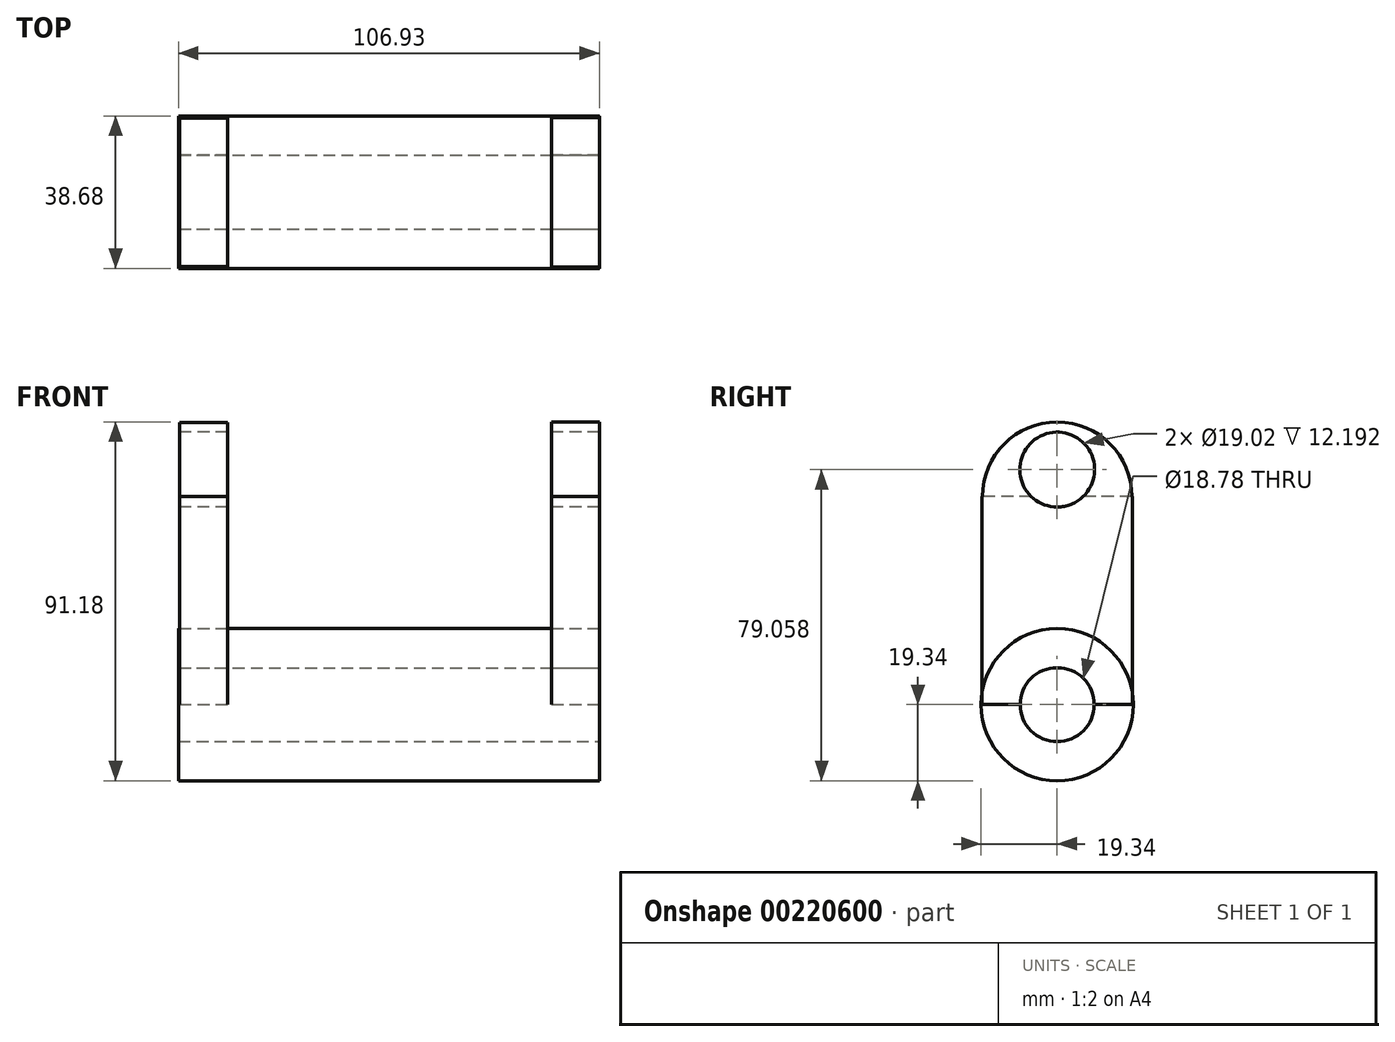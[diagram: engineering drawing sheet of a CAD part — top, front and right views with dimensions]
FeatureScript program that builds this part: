
annotation { "Feature Type Name" : "Feature", "Feature Type Description" : "" }
export const myFeature = defineFeature(function(context is Context, id is Id, definition is map)
    precondition{}
    {
        {
            var Q0;
            Q0=qCreatedBy(makeId("Top.planeOp"),FACE);
            var sketch = newSketch(context, id + "F0", { "sketchPlane" : qUnion([Q0])});
            skLineSegment(sketch, "E0.bottom", {"start": v(41.16, 19.13) * mm, "end": v(53.34, 19.13) * mm});
            skLineSegment(sketch, "E0.top", {"start": v(41.16, -19.13) * mm, "end": v(53.34, -19.13) * mm});
            skLineSegment(sketch, "E0.left", {"start": v(41.16, 19.13) * mm, "end": v(41.16, -19.13) * mm});
            skLineSegment(sketch, "E0.right", {"start": v(53.34, 19.13) * mm, "end": v(53.34, -19.13) * mm});
            skPoint(sketch, "E0.middle", {"position": v(47.25, 0) * mm});
            skLineSegment(sketch, "E1.MirrorCS", {"start": v(-41.16, 19.13) * mm, "end": v(-41.16, -19.13) * mm});
            skLineSegment(sketch, "E2.MirrorCS", {"start": v(-53.34, 19.13) * mm, "end": v(-53.34, -19.13) * mm});
            skLineSegment(sketch, "E3.MirrorCS", {"start": v(-41.16, 19.13) * mm, "end": v(-53.34, 19.13) * mm});
            skLineSegment(sketch, "E4.MirrorCS", {"start": v(-41.16, -19.13) * mm, "end": v(-53.34, -19.13) * mm});
            skSolve(sketch);
        }
        {
            var Q0;
            Q0=makeQuery(id+"F0.imprint","IMPRINT",FACE,{"disambiguationData":[TD([[makeQuery(id+"F0.imprint","IMPRINT",EDGE,{"derivedFrom":sQuery(id+"F0.wireOp",EDGE,"E0.bottom")}),-1.0]])]});
            var Q1;
            Q1=makeQuery(id+"F0.imprint","IMPRINT",FACE,{"disambiguationData":[TD([[makeQuery(id+"F0.imprint","IMPRINT",EDGE,{"derivedFrom":sQuery(id+"F0.wireOp",EDGE,"E1.MirrorCS")}),-1.0]])]});
            extrude(context, id + "F1", {"entities" : qUnion([Q0, Q1]), "depth" : 52.83 * mm});
        }
        {
            var Q0;
            Q0=makeQuery(id+"F1.opExtrude","SWEPT_FACE",FACE,{"disambiguationData":[OSD([sQuery(id+"F0.wireOp",EDGE,"E0.right")])]});
            var sketch = newSketch(context, id + "F2", { "sketchPlane" : qUnion([Q0])});
            skCircle(sketch, "E5", {"center": v(0, 0) * mm, "radius": 19.34 * mm});
            skSolve(sketch);
        }
        {
            var Q0;
            {var subQ1=sQuery(id+"F0.wireOp",EDGE,"E0.right");var subQ6=makeQuery(id+"F1.opExtrude","CAP_EDGE",EDGE,{"disambiguationData":[OSD([subQ1])],"isStart":true});Q0=makeQuery(id+"F2.imprint","IMPRINT",FACE,{"disambiguationData":[TD([[makeQuery(id+"F2.imprint","IMPRINT",EDGE,{"derivedFrom":subQ6}),-1.0]])]});}
            var Q1;
            {var subQ1=sQuery(id+"F0.wireOp",EDGE,"E0.right");var subQ6=makeQuery(id+"F1.opExtrude","CAP_EDGE",EDGE,{"disambiguationData":[OSD([subQ1])],"isStart":true});Q1=makeQuery(id+"F2.imprint","IMPRINT",FACE,{"disambiguationData":[TD([[makeQuery(id+"F2.imprint","IMPRINT",EDGE,{"derivedFrom":subQ6}),1.0]])]});}
            extrude(context, id + "F3", {"entities" : qUnion([Q0, Q1]), "oppositeDirection" : true, "depth" : 106.93 * mm});
        }
        {
            var Q0;
            Q0=makeQuery(id+"F1.opExtrude","SWEPT_FACE",FACE,{"disambiguationData":[OSD([sQuery(id+"F0.wireOp",EDGE,"E2.MirrorCS")])]});
            var sketch = newSketch(context, id + "F4", { "sketchPlane" : qUnion([Q0])});
            skCircle(sketch, "E6", {"center": v(0, 52.83) * mm, "radius": 18.89 * mm});
            skCircle(sketch, "E7", {"center": v(0, 52.83) * mm, "radius": 19.05 * mm});
            skSolve(sketch);
        }
        {
            var Q0;
            {var subQ0=sQuery(id+"F4.wireOp",EDGE,"E6");var subQ1=makeQuery(id+"F1.opExtrude","CAP_EDGE",EDGE,{"disambiguationData":[OSD([sQuery(id+"F0.wireOp",EDGE,"E2.MirrorCS")])],"isStart":false});var subQ2=makeQuery(id+"F4.imprint","INTERSECT",VERTEX,{"disambiguationData":[OD(0.0)],"derivedFrom":[subQ1,subQ0]});Q0=makeQuery(id+"F4.imprint","IMPRINT",FACE,{"disambiguationData":[TD([[makeQuery(id+"F4.imprint","IMPRINT",EDGE,{"disambiguationData":[TD([[subQ2,1.0]])],"derivedFrom":subQ0}),1.0]])]});}
            extrude(context, id + "F5", {"entities" : qUnion([Q0]), "operationType" : NewBodyOperationType.ADD, "oppositeDirection" : true, "depth" : 12.2 * mm});
        }
        {
            var Q0;
            Q0=makeQuery(id+"F1.opExtrude","SWEPT_FACE",FACE,{"disambiguationData":[OSD([sQuery(id+"F0.wireOp",EDGE,"E0.right")])]});
            var sketch = newSketch(context, id + "F6", { "sketchPlane" : qUnion([Q0])});
            skCircle(sketch, "E8", {"center": v(0, 52.83) * mm, "radius": 19 * mm});
            skSolve(sketch);
        }
        {
            var Q0;
            {var subQ0=sQuery(id+"F6.wireOp",EDGE,"E8");var subQ1=makeQuery(id+"F1.opExtrude","CAP_EDGE",EDGE,{"disambiguationData":[OSD([sQuery(id+"F0.wireOp",EDGE,"E0.right")])],"isStart":false});var subQ2=makeQuery(id+"F6.imprint","INTERSECT",VERTEX,{"disambiguationData":[OD(0.0)],"derivedFrom":[subQ1,subQ0]});Q0=makeQuery(id+"F6.imprint","IMPRINT",FACE,{"disambiguationData":[TD([[makeQuery(id+"F6.imprint","IMPRINT",EDGE,{"disambiguationData":[TD([[subQ2,-1.0]])],"derivedFrom":subQ0}),1.0]])]});}
            extrude(context, id + "F7", {"entities" : qUnion([Q0]), "operationType" : NewBodyOperationType.ADD, "oppositeDirection" : true, "depth" : 12.2 * mm});
        }
        {
            var Q0;
            {var subQ0=sQuery(id+"F0.wireOp",EDGE,"E2.MirrorCS");Q0=makeQuery(id+"F5.boolean.opBoolean","MERGE",FACE,{"derivedFrom":[makeQuery(id+"F1.opExtrude","SWEPT_FACE",FACE,{"disambiguationData":[OSD([subQ0])]}),makeQuery(id+"F5.opExtrude","CAP_FACE",FACE,{"disambiguationData":[OSD([subQ0,sQuery(id+"F4.wireOp",EDGE,"E6")])],"isStart":true})]});}
            var sketch = newSketch(context, id + "F8", { "sketchPlane" : qUnion([Q0])});
            skCircle(sketch, "E9", {"center": v(0, 0) * mm, "radius": 9.65 * mm});
            skCircle(sketch, "E10", {"center": v(0, 59.72) * mm, "radius": 9.5 * mm});
            skPoint(sketch, "E10.centerSnap0", {"position": v(0, 71.72) * mm});
            skSolve(sketch);
        }
        {
            var Q0;
            Q0=makeQuery(id+"F8.imprint","IMPRINT",FACE,{"disambiguationData":[TD([[makeQuery(id+"F8.imprint","IMPRINT",EDGE,{"derivedFrom":sQuery(id+"F8.wireOp",EDGE,"E10")}),1.0]])]});
            extrude(context, id + "F9", {"entities" : qUnion([Q0]), "operationType" : NewBodyOperationType.REMOVE, "oppositeDirection" : true, "depth" : 119.13 * mm});
        }
        {
            var Q0;
            Q0=makeQuery(id+"F3.opExtrude","CAP_FACE",FACE,{"disambiguationData":[OSD([sQuery(id+"F2.wireOp",EDGE,"E5")])],"isStart":true});
            var sketch = newSketch(context, id + "F10", { "sketchPlane" : qUnion([Q0])});
            skCircle(sketch, "E11", {"center": v(0, 0) * mm, "radius": 9.39 * mm});
            skSolve(sketch);
        }
        {
            var Q0;
            Q0=makeQuery(id+"F10.imprint","IMPRINT",FACE,{"disambiguationData":[TD([[makeQuery(id+"F10.imprint","IMPRINT",EDGE,{"derivedFrom":sQuery(id+"F10.wireOp",EDGE,"E11")}),1.0]])]});
            extrude(context, id + "F11", {"entities" : qUnion([Q0]), "operationType" : NewBodyOperationType.REMOVE, "endBound" : BoundingType.THROUGH_ALL, "oppositeDirection" : true, "depth" : 25.4 * mm});
        }
    });
